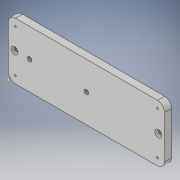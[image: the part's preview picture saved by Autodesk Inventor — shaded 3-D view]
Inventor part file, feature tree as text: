
AUTODESK INVENTOR PART (.ipt)
format: ipt  version: 2018 (Build 220112000, 112)  size: 129,024 bytes
history: native  units: in
note: dims shown in document units (in); Inventor stores cm internally (conversion verified against a paired STEP export)
features: sketch x5, hole x3, extrude x1
ambient origin geometry x8: Origin, YZ Plane, XZ Plane, XY Plane, X Axis, Y Axis, Z Axis, Center Point
bodies: Solid1 (feature_tree)
feature tree (9):
  sketch  "Sketch1"  dims[d0=11.0in d1=4.0in]
  extrude  "Extrusion1"  Depth=4.0in
  sketch  "Sketch2"  dims[d2=0.125in d3=0.5in]
  sketch  "Sketch3"  dims[d4=0.5in d5=0.0in d6=0.436in]
  hole  "Hole1"  [1 undecoded]
  hole  "Hole2"  [1 undecoded]
  sketch  "Sketch4"  dims[d7=1.5in d8=5.5in]
  sketch  "Sketch5"  dims[d9=0.438in d10=2.0in d11=2.0in d12=2.0in d13=2.0in d14=0.25in d15=0.75in d16=0.5in d17=0.25in d18=0.5635in d19=1.0in d20=0.8108in d21=0.3125in d22=0.75in d23=0.5in d24=0.25in d25=0.5635in d26=1.0in d27=0.8108in d28=0.5in d29=0.13in d30=0.328in d31=0.5in d32=0.25in d33=0.5635in d34=0.484in d35=0.8108in]
  hole  "Hole3"  [1 undecoded]
note: 3 required parameter values undecoded (feature->parameter linkage not recoverable at this tier; creation-order binding heuristic only, values carry confidence <= 0.55)
